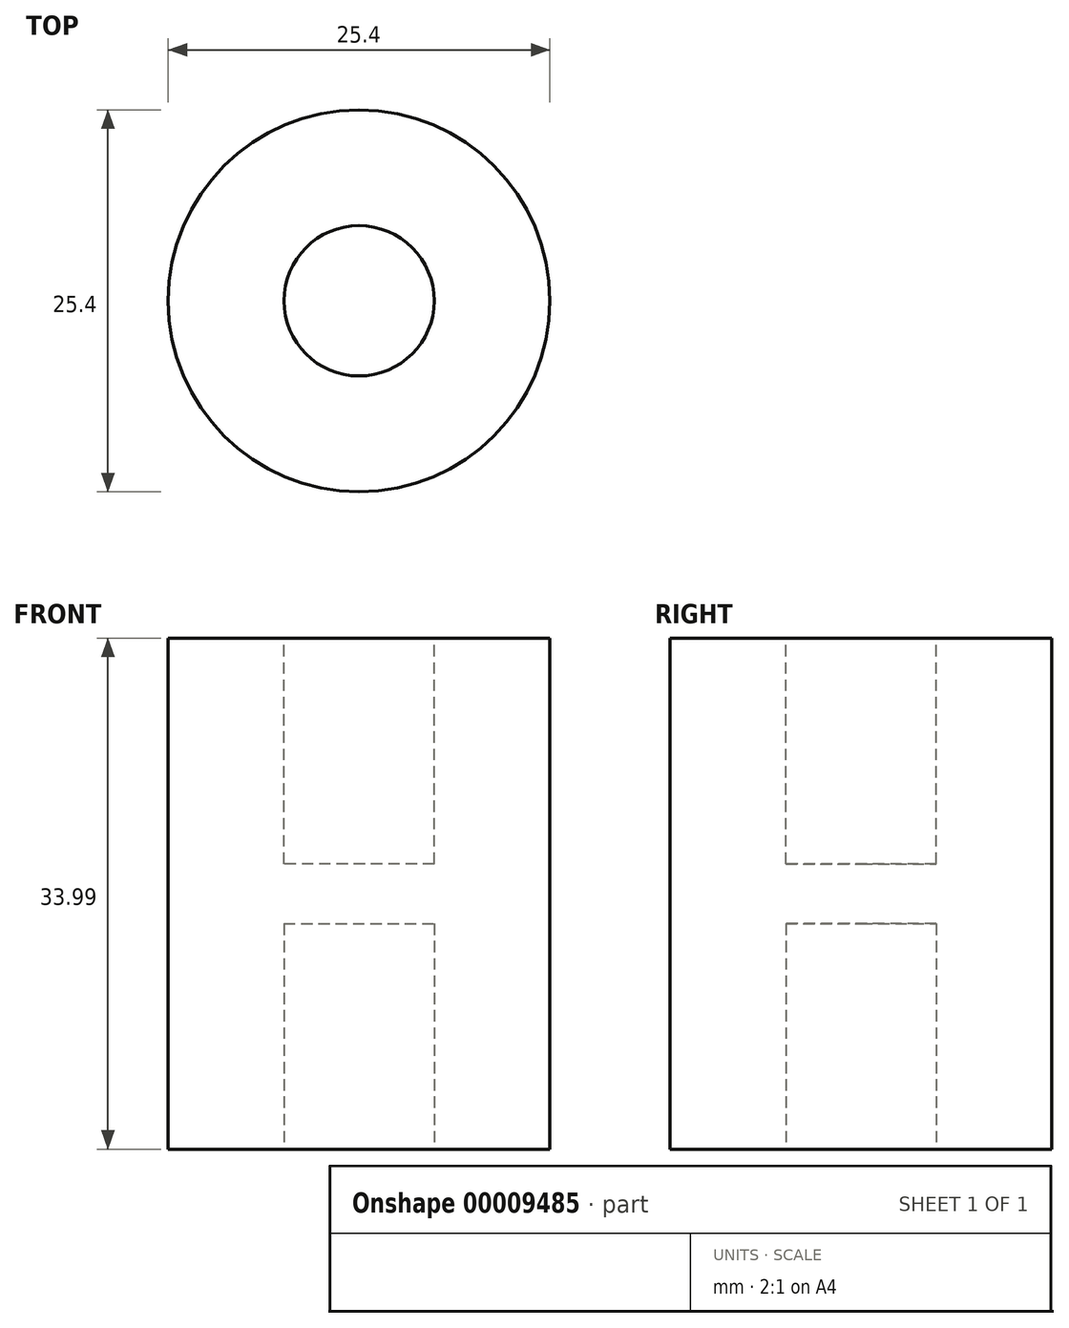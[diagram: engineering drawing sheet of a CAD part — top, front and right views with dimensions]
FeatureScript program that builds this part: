
annotation { "Feature Type Name" : "Feature", "Feature Type Description" : "" }
export const myFeature = defineFeature(function(context is Context, id is Id, definition is map)
    precondition{}
    {
        {
            var Q0;
            Q0=qCreatedBy(makeId("Top.planeOp"),FACE);
            var sketch = newSketch(context, id + "F0", { "sketchPlane" : qUnion([Q0])});
            skCircle(sketch, "E0", {"center": v(0, 0) * mm, "radius": 12.7 * mm});
            skSolve(sketch);
        }
        {
            var Q0;
            Q0=makeQuery(id+"F0.imprint","IMPRINT",FACE,{"disambiguationData":[TD([[makeQuery(id+"F0.imprint","IMPRINT",EDGE,{"derivedFrom":sQuery(id+"F0.wireOp",EDGE,"E0")}),1.0]])]});
            extrude(context, id + "F1", {"entities" : qUnion([Q0]), "depth" : 34 * mm});
        }
        {
            var Q0;
            Q0=makeQuery(id+"F1.opExtrude","CAP_FACE",FACE,{"disambiguationData":[OSD([sQuery(id+"F0.wireOp",EDGE,"E0")])],"isStart":false});
            var sketch = newSketch(context, id + "F2", { "sketchPlane" : qUnion([Q0])});
            skCircle(sketch, "E1", {"center": v(0, 0) * mm, "radius": 5 * mm});
            skSolve(sketch);
        }
        {
            var Q0;
            Q0=makeQuery(id+"F2.imprint","IMPRINT",FACE,{"disambiguationData":[TD([[makeQuery(id+"F2.imprint","IMPRINT",EDGE,{"derivedFrom":sQuery(id+"F2.wireOp",EDGE,"E1")}),1.0]])]});
            extrude(context, id + "F3", {"entities" : qUnion([Q0]), "operationType" : NewBodyOperationType.REMOVE, "oppositeDirection" : true, "depth" : 15 * mm});
        }
        {
            var Q0;
            Q0=makeQuery(id+"F1.opExtrude","CAP_FACE",FACE,{"disambiguationData":[OSD([sQuery(id+"F0.wireOp",EDGE,"E0")])],"isStart":true});
            var sketch = newSketch(context, id + "F4", { "sketchPlane" : qUnion([Q0])});
            skCircle(sketch, "E2", {"center": v(0, 0) * mm, "radius": 5 * mm});
            skSolve(sketch);
        }
        {
            var Q0;
            Q0=makeQuery(id+"F4.imprint","IMPRINT",FACE,{"disambiguationData":[TD([[makeQuery(id+"F4.imprint","IMPRINT",EDGE,{"derivedFrom":sQuery(id+"F4.wireOp",EDGE,"E2")}),1.0]])]});
            extrude(context, id + "F5", {"entities" : qUnion([Q0]), "operationType" : NewBodyOperationType.REMOVE, "oppositeDirection" : true, "depth" : 15 * mm});
        }
    });
